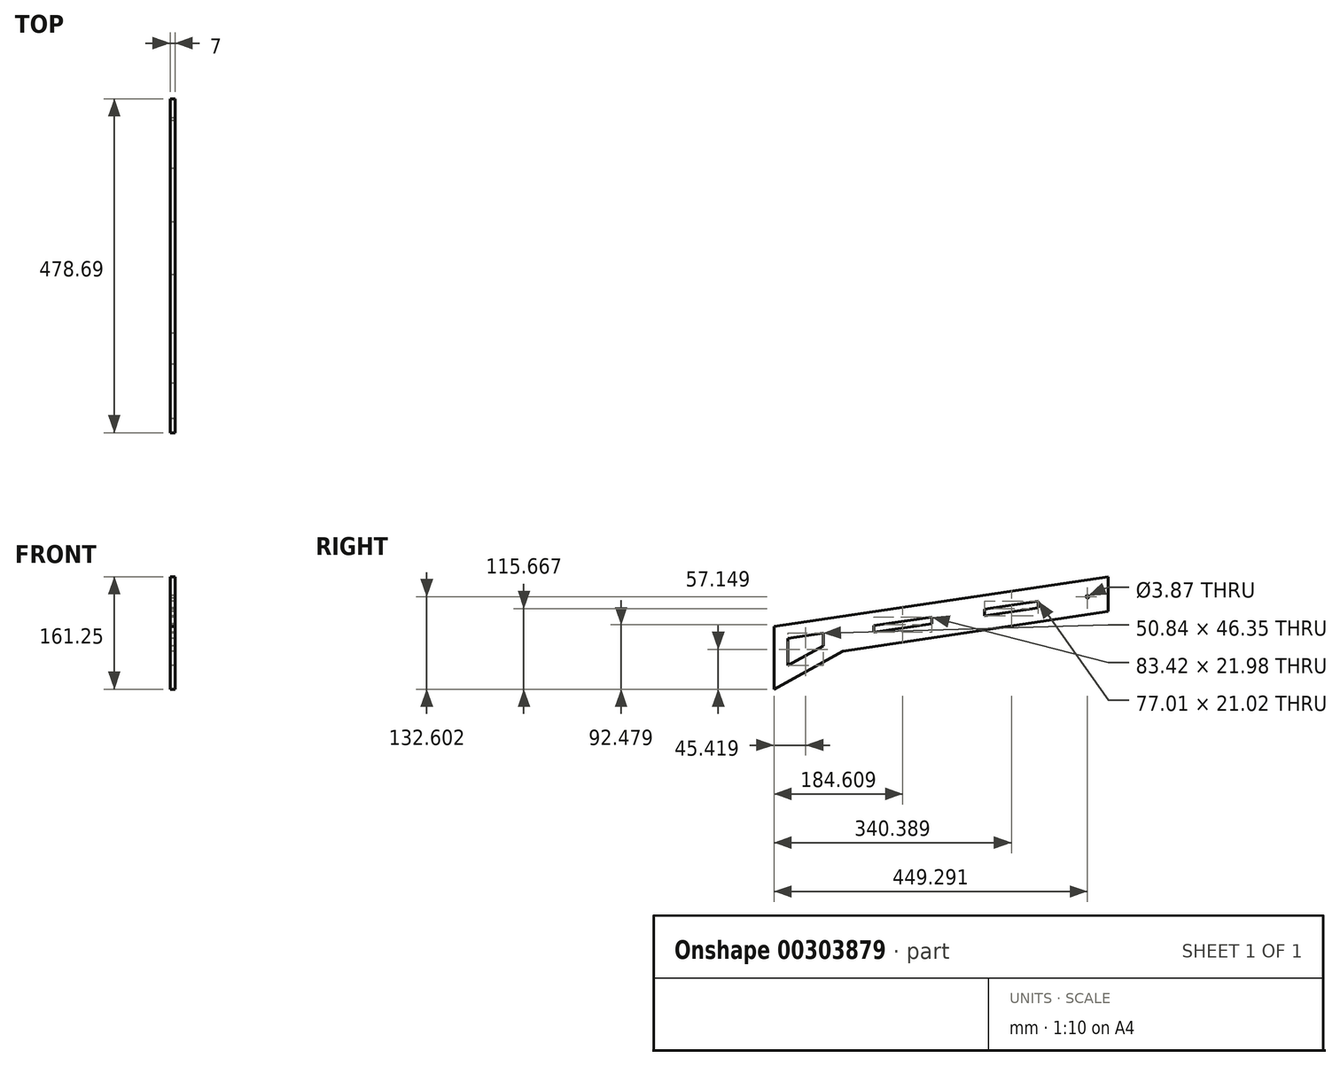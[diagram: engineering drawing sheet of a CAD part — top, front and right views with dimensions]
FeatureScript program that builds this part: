
annotation { "Feature Type Name" : "Feature", "Feature Type Description" : "" }
export const myFeature = defineFeature(function(context is Context, id is Id, definition is map)
    precondition{}
    {
        {
            var Q0;
            Q0=qCreatedBy(makeId("Right.planeOp"),FACE);
            var sketch = newSketch(context, id + "F0", { "sketchPlane" : qUnion([Q0])});
            skLineSegment(sketch, "E0.bottom", {"start": v(-331.58, 177.92) * mm, "end": v(147.11, 249.17) * mm});
            skLineSegment(sketch, "E0.left", {"start": v(-331.58, 177.92) * mm, "end": v(-331.58, 87.92) * mm});
            skLineSegment(sketch, "E0.right", {"start": v(147.11, 249.17) * mm, "end": v(147.11, 199.17) * mm});
            skLineSegment(sketch, "E1", {"start": v(-331.58, 87.92) * mm, "end": v(-233.12, 142.57) * mm});
            skLineSegment(sketch, "E2", {"start": v(-233.12, 142.57) * mm, "end": v(147.11, 199.17) * mm});
            skLineSegment(sketch, "E3.1", {"start": v(-311.58, 160.68) * mm, "end": v(-260.74, 168.24) * mm});
            skLineSegment(sketch, "E3.2", {"start": v(-188.68, 169.41) * mm, "end": v(-105.26, 181.83) * mm});
            skLineSegment(sketch, "E3.3", {"start": v(-311.58, 121.9) * mm, "end": v(-260.74, 150.12) * mm});
            skLineSegment(sketch, "E3.4", {"start": v(-311.58, 160.68) * mm, "end": v(-311.58, 121.9) * mm});
            skLineSegment(sketch, "E4", {"start": v(-260.74, 150.12) * mm, "end": v(-260.74, 168.24) * mm});
            skLineSegment(sketch, "E5", {"start": v(-188.68, 178.97) * mm, "end": v(-188.68, 169.41) * mm});
            skLineSegment(sketch, "E6", {"start": v(-105.26, 191.39) * mm, "end": v(-105.26, 181.83) * mm});
            skLineSegment(sketch, "E7", {"start": v(-29.7, 202.64) * mm, "end": v(-29.7, 193.08) * mm});
            skLineSegment(sketch, "E8", {"start": v(47.31, 214.1) * mm, "end": v(47.31, 204.54) * mm});
            skLineSegment(sketch, "E9.trimOffspring", {"start": v(-188.68, 178.97) * mm, "end": v(-105.26, 191.39) * mm});
            skLineSegment(sketch, "E10.trimOffspring", {"start": v(-29.7, 202.64) * mm, "end": v(47.31, 214.1) * mm});
            skLineSegment(sketch, "E11.trimOffspring", {"start": v(-29.7, 193.08) * mm, "end": v(47.31, 204.54) * mm});
            skCircle(sketch, "E12", {"center": v(117.71, 220.52) * mm, "radius": 1.94 * mm});
            skSolve(sketch);
        }
        {
            var Q0;
            Q0=makeQuery(id+"F0.imprint","IMPRINT",FACE,{"disambiguationData":[TD([[makeQuery(id+"F0.imprint","IMPRINT",EDGE,{"derivedFrom":sQuery(id+"F0.wireOp",EDGE,"E0.bottom")}),-1.0]])]});
            extrude(context, id + "F1", {"entities" : qUnion([Q0]), "depth" : 7 * mm});
        }
    });
